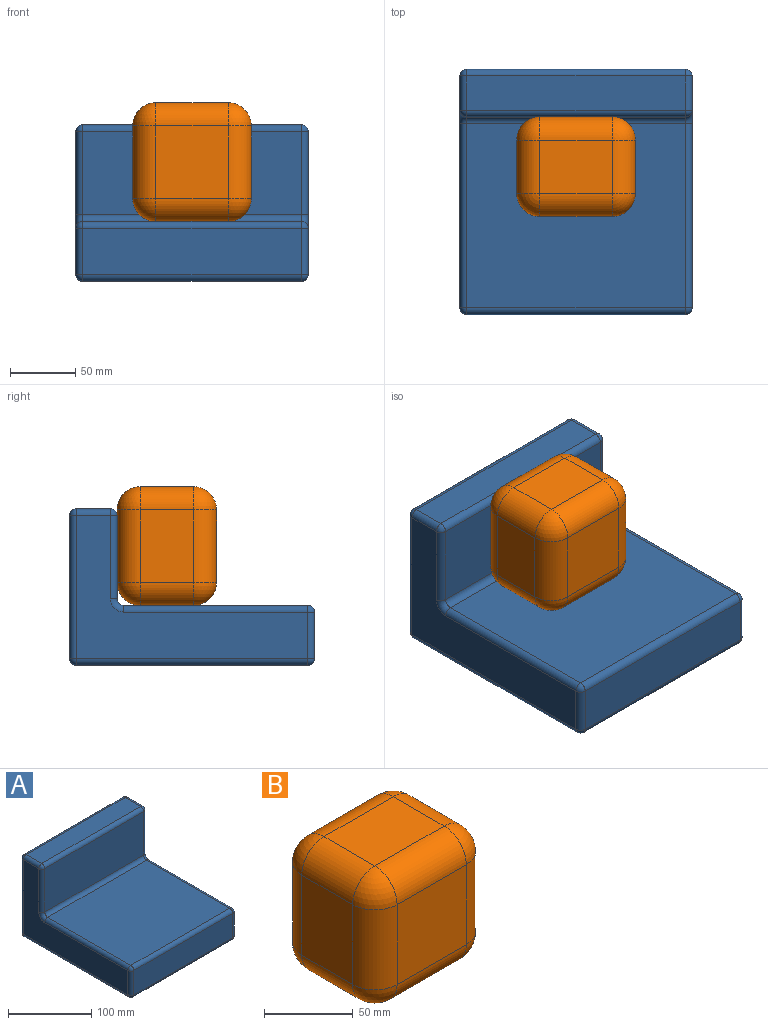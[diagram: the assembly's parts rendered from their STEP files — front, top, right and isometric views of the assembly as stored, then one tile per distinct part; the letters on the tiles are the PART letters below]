
ASSEMBLY  parts=2 mates=2
PART A: 38 faces, bbox 177.8x187.7x119.7 mm
  f0: plane 167.64x26.26mm, normal (0,0,1), area 4402.4mm2, adj f26,f31,f34,f37
  f1: plane 167.64x63.73mm, normal (0,-1,0), area 10683.9mm2, adj f23,f32,f33,f37
  f2: plane 167.64x141.09mm, normal (0,0,1), area 23651.5mm2, adj f13,f22,f23,f24
  f3: plane 167.64x35.64mm, normal (0,-1,0), area 5975.5mm2, adj f8,f12,f13,f14
  f4: plane 177.51x167.64mm, normal (0,0,-1), area 29757.2mm2, adj f8,f11,f15,f16
  f5: plane 167.64x109.54mm, normal (0,1,0), area 18362.6mm2, adj f16,f21,f25,f26
  f6: plane 177.51x109.54mm, normal (1,0,0), area 8289.8mm2, adj f11,f12,f21,f22,f28,f31,f32
  f7: plane 177.51x109.54mm, normal (-1,0,0), area 8289.8mm2, adj f14,f15,f24,f25,f29,f33,f34
  f8: cylinder r=5.08mm len=167.64mm, axis (-1,0,0), area 1337.7mm2, adj f3,f4,f9,f10
  f9: sphere r=5.08mm, area 40.5mm2, adj f8,f11,f12
  f10: sphere r=5.08mm, area 40.5mm2, adj f8,f14,f15
  f11: cylinder r=5.08mm len=177.51mm, axis (0,-1,0), area 1416.4mm2, adj f4,f6,f9,f17
  f12: cylinder r=5.08mm len=35.64mm, axis (0,0,1), area 284.4mm2, adj f3,f6,f9,f18
  f13: cylinder r=5.08mm len=167.64mm, axis (-1,0,0), area 1337.7mm2, adj f2,f3,f18,f19
  f14: cylinder r=5.08mm len=35.64mm, axis (0,0,-1), area 284.4mm2, adj f3,f7,f10,f19
  f15: cylinder r=5.08mm len=177.51mm, axis (0,1,0), area 1416.4mm2, adj f4,f7,f10,f20
  f16: cylinder r=5.08mm len=167.64mm, axis (-1,0,0), area 1337.7mm2, adj f4,f5,f17,f20
  f17: sphere r=5.08mm, area 40.5mm2, adj f11,f16,f21
  f18: sphere r=5.08mm, area 40.5mm2, adj f12,f13,f22
  f19: sphere r=5.08mm, area 40.5mm2, adj f13,f14,f24
  f20: sphere r=5.08mm, area 40.5mm2, adj f15,f16,f25
  f21: cylinder r=5.08mm len=109.54mm, axis (0,0,-1), area 874.1mm2, adj f5,f6,f17,f27
  f22: cylinder r=5.08mm len=141.09mm, axis (0,1,0), area 1125.8mm2, adj f2,f6,f18,f28
  f23: cylinder r=5.08mm len=167.64mm, axis (1,0,0), area 1337.7mm2, adj f1,f2,f28,f29
  f24: cylinder r=5.08mm len=141.09mm, axis (0,-1,0), area 1125.8mm2, adj f2,f7,f19,f29
  f25: cylinder r=5.08mm len=109.54mm, axis (0,0,1), area 874.1mm2, adj f5,f7,f20,f30
  f26: cylinder r=5.08mm len=167.64mm, axis (-1,0,0), area 1337.7mm2, adj f0,f5,f27,f30
  f27: sphere r=5.08mm, area 40.5mm2, adj f21,f26,f31
  f28: torus R=10.16mm, axis (1,0,0), area 86.8mm2, adj f6,f22,f23,f32
  f29: torus R=10.16mm, axis (1,0,0), area 86.8mm2, adj f7,f23,f24,f33
  f30: sphere r=5.08mm, area 40.5mm2, adj f25,f26,f34
  f31: cylinder r=5.08mm len=26.26mm, axis (0,1,0), area 209.6mm2, adj f0,f6,f27,f35
  f32: cylinder r=5.08mm len=63.73mm, axis (0,0,1), area 508.6mm2, adj f1,f6,f28,f35
  f33: cylinder r=5.08mm len=63.73mm, axis (0,0,-1), area 508.6mm2, adj f1,f7,f29,f36
  f34: cylinder r=5.08mm len=26.26mm, axis (0,-1,0), area 209.6mm2, adj f0,f7,f30,f36
  f35: sphere r=5.08mm, area 40.5mm2, adj f31,f32,f37
  f36: sphere r=5.08mm, area 40.5mm2, adj f33,f34,f37
  f37: cylinder r=5.08mm len=167.64mm, axis (-1,0,0), area 1337.7mm2, adj f0,f1,f35,f36
PART B: 26 faces, bbox 90.9x76.2x90.9 mm
  f0: plane 55.32x40.64mm, normal (0,0,1), area 2248.1mm2, adj f14,f19,f22,f25
  f1: plane 55.32x40.64mm, normal (-1,0,0), area 2248.1mm2, adj f11,f20,f21,f25
  f2: plane 55.32x40.64mm, normal (0,0,-1), area 2248.1mm2, adj f6,f10,f11,f12
  f3: plane 55.32x40.64mm, normal (1,0,0), area 2248.1mm2, adj f6,f9,f13,f14
  f4: plane 55.32x55.32mm, normal (0,-1,0), area 3059.9mm2, adj f9,f10,f19,f20
  f5: plane 55.32x55.32mm, normal (0,1,0), area 3059.9mm2, adj f12,f13,f21,f22
  f6: cylinder r=17.78mm len=40.64mm, axis (0,-1,0), area 1135mm2, adj f2,f3,f7,f8
  f7: sphere r=17.78mm, area 496.6mm2, adj f6,f9,f10
  f8: sphere r=17.78mm, area 496.6mm2, adj f6,f12,f13
  f9: cylinder r=17.78mm len=55.32mm, axis (0,0,-1), area 1544.9mm2, adj f3,f4,f7,f15
  f10: cylinder r=17.78mm len=55.32mm, axis (-1,0,0), area 1544.9mm2, adj f2,f4,f7,f16
  f11: cylinder r=17.78mm len=40.64mm, axis (0,1,0), area 1135mm2, adj f1,f2,f16,f17
  f12: cylinder r=17.78mm len=55.32mm, axis (1,0,0), area 1544.9mm2, adj f2,f5,f8,f17
  f13: cylinder r=17.78mm len=55.32mm, axis (0,0,1), area 1544.9mm2, adj f3,f5,f8,f18
  f14: cylinder r=17.78mm len=40.64mm, axis (0,1,0), area 1135mm2, adj f0,f3,f15,f18
  f15: sphere r=17.78mm, area 496.6mm2, adj f9,f14,f19
  f16: sphere r=17.78mm, area 496.6mm2, adj f10,f11,f20
  f17: sphere r=17.78mm, area 496.6mm2, adj f11,f12,f21
  f18: sphere r=17.78mm, area 496.6mm2, adj f13,f14,f22
  f19: cylinder r=17.78mm len=55.32mm, axis (1,0,0), area 1544.9mm2, adj f0,f4,f15,f23
  f20: cylinder r=17.78mm len=55.32mm, axis (0,0,1), area 1544.9mm2, adj f1,f4,f16,f23
  f21: cylinder r=17.78mm len=55.32mm, axis (0,0,-1), area 1544.9mm2, adj f1,f5,f17,f24
  f22: cylinder r=17.78mm len=55.32mm, axis (-1,0,0), area 1544.9mm2, adj f0,f5,f18,f24
  f23: sphere r=17.78mm, area 496.6mm2, adj f19,f20,f25
  f24: sphere r=17.78mm, area 496.6mm2, adj f21,f22,f25
  f25: cylinder r=17.78mm len=40.64mm, axis (0,-1,0), area 1135mm2, adj f0,f1,f23,f24
PLACE A t=(-64.79,-62.45,-18.42)mm
PLACE B t=(22.7,20.59,30.28)mm
MATE planar B.f2 <-> A.f2  axis (0,0,-1) through (24.11,-17.51,-41.73)mm
MATE planar A.f1 <-> B.f5  axis (0,-1,0) through (24.11,20.59,-4.78)mm
